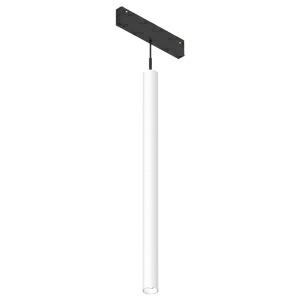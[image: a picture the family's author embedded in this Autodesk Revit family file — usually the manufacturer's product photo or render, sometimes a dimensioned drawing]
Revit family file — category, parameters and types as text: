
# Revit family: 2look4_25_magtrack_hangover_plug_o30_l450_insert_led_7w__4000k__48v__cri90_810-0438_2f55
name_source: partatom
category: Leuchten
revit_build: Autodesk Revit 2016 (Build: 20190508_0715(x64)
units: mm (PartAtom-declared; Revit-internal decimal feet)

## family parameters
Basisbauteil = Fläche
Beim Laden mit Abzugskörper schneiden = Nein
Bemaßung runder Anschluss = Durchmesser verwenden
Gemeinsam genutzt = Nein
Lichtquelle = Nein
Raumberechnungspunkt = Nein
Teiletyp = Normal

## types (1)
- 810-0438-K24 (1 x LED, 513.92 lm, 6.4 W, 4000K)
    Beschreibung = The spot-insert 2LOOK4 25 MAGTRACK / 2LOOK4 50 MAGTRACK / HYPRO from the familiy 2LOOK4 consists of aluminum. The ballast is integrated and allows for an operation with 48V. 2LOOK4 25 MAGTRACK / 2LOOK4 50 MAGTRACK / HYPRO (# 810-0438) ist not dimmable (on/off). The lens based solution shows clear limits and creates sharp contours.
    CIE Flux Codes = 99 100 100 100 74
    Color Rendering = 1A/90…99
    Color Temperature = 4000K
    Height = 0 mm  [stored 0 ft]
    Hersteller = Prolicht
    Lamp Light Flux = 513.92 lm
    Lamp Power = 6.4 W
    Lamp count = 1
    Lampe = 1 x LED
    Length = 28 mm
    Luminous efficacy = 59 lm/W
    ModVariant = Nein
    Modell = 810-0438
    Mounting Place = Ceiling
    Mounting Type = Recessed
    Number of Poles = 1
    OnlyDefault = Ja
    Power Factor = 1
    Product Name = 2LOOK4 25 MAGTRACK__HANGOVER PLUG Ø30 L450 insert LED 7W  4000K  48V  CRI90
    Product group = Trimless recessed profile systems
    ProductGroupID = 414
    Protection Class = Protection class
    Protection Degree = Degree of protection
    RLX_Detail_Level = 1
    RlxData = <blob elided: 39025 chars, md5=6467df04>
    Scheinlast = 6 VA
    Socket = socket
    Standby Power = 0 W
    System Light Flux = 379 lm
    System Power = 6 W
    Typenbild = 810-0438.jpg
    URL = http://relux.com
    VarID = 810-0438-k24
    Voltage = 0 V
    Vorgabe-Ansicht = 1800 mm
    Weight = 0.00 kg
    Width = 0 mm  [stored 0 ft]

note: [stored X ft] marks values corroborated as IEEE doubles in the binary element streams (Revit-internal decimal feet)

## geometry (parser evidence)
native form markers: Sweep x9
no freeform markers — native parametric forms only
